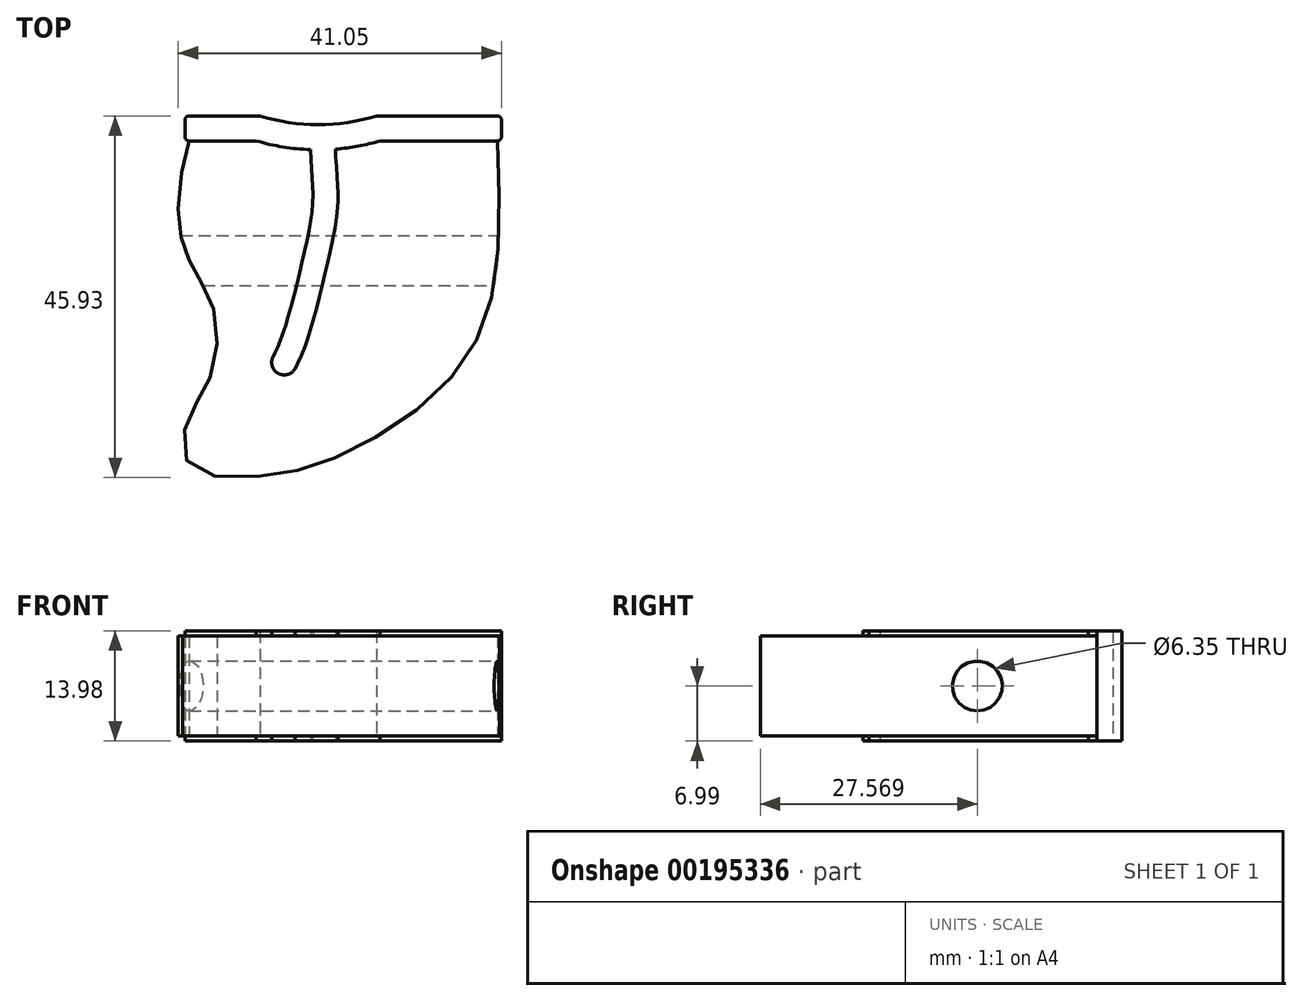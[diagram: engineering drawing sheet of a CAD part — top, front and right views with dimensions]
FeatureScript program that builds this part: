
annotation { "Feature Type Name" : "Feature", "Feature Type Description" : "" }
export const myFeature = defineFeature(function(context is Context, id is Id, definition is map)
    precondition{}
    {
        {
            var Q0;
            Q0=qCreatedBy(makeId("Top.planeOp"),FACE);
            var sketch = newSketch(context, id + "F0", { "sketchPlane" : qUnion([Q0])});
            skLineSegment(sketch, "E0", {"start": v(-17.53, 0) * mm, "end": v(-8.51, 0) * mm});
            skLineSegment(sketch, "E1", {"start": v(6.28, 0) * mm, "end": v(21.65, 0) * mm});
            skLineSegment(sketch, "E2.0", {"start": v(6.75, -3.17) * mm, "end": v(21.65, -3.17) * mm});
            skLineSegment(sketch, "E2.2", {"start": v(-17.53, -3.18) * mm, "end": v(-8.98, -3.18) * mm});
            skLineSegment(sketch, "E3", {"start": v(-18.04, -0.5) * mm, "end": v(-18.04, -2.67) * mm});
            skLineSegment(sketch, "E4", {"start": v(22.16, -0.5) * mm, "end": v(22.16, -2.67) * mm});
            skPoint(sketch, "E5.visualSharp", {"position": v(-18.04, -3.18) * mm});
            skArc(sketch, "E5.filletArc", {"start": v(-18.04, -2.67) * mm, "mid": v(-17.89, -3.03) * mm, "end": v(-17.53, -3.18) * mm});
            skPoint(sketch, "E6.visualSharp", {"position": v(-18.04, 0) * mm});
            skArc(sketch, "E6.filletArc", {"start": v(-17.53, 0) * mm, "mid": v(-17.89, -0.15) * mm, "end": v(-18.04, -0.5) * mm});
            skPoint(sketch, "E7.visualSharp", {"position": v(6.28, 0) * mm});
            skPoint(sketch, "E8.visualSharp", {"position": v(-8.51, 0) * mm});
            skPoint(sketch, "E9.visualSharp", {"position": v(22.16, 0) * mm});
            skArc(sketch, "E9.filletArc", {"start": v(22.16, -0.5) * mm, "mid": v(22, -0.15) * mm, "end": v(21.65, 0) * mm});
            skPoint(sketch, "E10.visualSharp", {"position": v(22.16, -3.17) * mm});
            skArc(sketch, "E10.filletArc", {"start": v(21.65, -3.17) * mm, "mid": v(22, -3.03) * mm, "end": v(22.16, -2.67) * mm});
            skFitSpline(sketch, "E11", {"points": [v(-2.09, -4.28) * mm, v(-1.8, -10.72) * mm, v(-3.13, -18.5) * mm, v(-5.58, -27.62) * mm, v(-6.9, -30.73) * mm], "startDerivative": vector(0.81, -30.4) * mm, "endDerivative": vector(-7.37, -14.95) * mm});
            skFitSpline(sketch, "E12.0", {"points": [v(1.09, -4.2) * mm, v(1.1, -4.78) * mm, v(1.16, -5.88) * mm, v(1.27, -7.2) * mm, v(1.34, -8.29) * mm, v(1.38, -9.13) * mm, v(1.4, -9.86) * mm, v(1.39, -10.46) * mm, v(1.37, -11.08) * mm, v(1.32, -11.85) * mm, v(1.2, -13.1) * mm, v(0.95, -14.66) * mm, v(0.57, -16.57) * mm, v(0.2, -18.2) * mm, v(-0.11, -19.55) * mm, v(-0.44, -20.93) * mm, v(-0.88, -22.7) * mm, v(-1.41, -24.78) * mm, v(-1.87, -26.4) * mm, v(-2.23, -27.61) * mm, v(-2.5, -28.46) * mm, v(-2.78, -29.23) * mm, v(-3.14, -30.16) * mm, v(-3.58, -31.16) * mm, v(-3.9, -31.82) * mm, v(-4.06, -32.13) * mm]});
            skArc(sketch, "E13", {"start": v(-6.9, -30.73) * mm, "mid": v(-6.13, -32.74) * mm, "end": v(-4.06, -32.13) * mm});
            skArc(sketch, "E14", {"start": v(-8.51, 0) * mm, "mid": v(-1.12, -1.13) * mm, "end": v(6.28, 0) * mm});
            skArc(sketch, "E15.0", {"start": v(-8.98, -3.18) * mm, "mid": v(-1.12, -4.3) * mm, "end": v(6.75, -3.18) * mm});
            skSolve(sketch);
        }
        {
            var Q0;
            Q0 = qSketchRegion(id + "F0", true);
            extrude(context, id + "F1", {"entities" : qUnion([Q0]), "endBound" : BoundingType.SYMMETRIC, "depth" : 13.97 * mm});
        }
        {
            var Q0;
            Q0=qCreatedBy(makeId("Top.planeOp"),FACE);
            var sketch = newSketch(context, id + "F2", { "sketchPlane" : qUnion([Q0])});
            skLineSegment(sketch, "E16", {"start": v(6.75, -3.17) * mm, "end": v(6.75, -3.17) * mm});
            skLineSegment(sketch, "E17", {"start": v(-17.53, -3.18) * mm, "end": v(-17.53, -3.18) * mm});
            skFitSpline(sketch, "E18", {"points": [v(-17.53, -3.18) * mm, v(-18.87, -11.15) * mm, v(-18.3, -16.34) * mm, v(-16.52, -20.17) * mm, v(-14.2, -25.3) * mm, v(-14.86, -33.3) * mm, v(-17.53, -38.15) * mm, v(-17.53, -44.2) * mm, v(-8.2, -45.76) * mm, v(2.25, -42.87) * mm, v(15.14, -33.98) * mm, v(21.14, -21.97) * mm, v(21.65, -3.17) * mm], "startDerivative": vector(-25.65, -67.95) * mm, "endDerivative": vector(-6.15, 159.47) * mm});
            skLineSegment(sketch, "E19", {"start": v(-17.53, -3.18) * mm, "end": v(-8.98, -3.18) * mm});
            skLineSegment(sketch, "E20", {"start": v(21.65, -3.18) * mm, "end": v(6.75, -3.17) * mm});
            skArc(sketch, "E21", {"start": v(-8.98, -3.18) * mm, "mid": v(-1.12, -4.18) * mm, "end": v(6.75, -3.17) * mm});
            skSolve(sketch);
        }
        {
            var Q0;
            Q0 = qSketchRegion(id + "F2", true);
            extrude(context, id + "F3", {"entities" : qUnion([Q0]), "operationType" : NewBodyOperationType.ADD, "endBound" : BoundingType.SYMMETRIC, "depth" : 12.7 * mm});
        }
        {
            var Q0;
            Q0=qCreatedBy(makeId("Right.planeOp"),FACE);
            var sketch = newSketch(context, id + "F4", { "sketchPlane" : qUnion([Q0])});
            skCircle(sketch, "E22", {"center": v(-18.36, 0) * mm, "radius": 3.18 * mm});
            skSolve(sketch);
        }
        {
            var Q0;
            Q0 = qSketchRegion(id + "F4", true);
            extrude(context, id + "F5", {"entities" : qUnion([Q0]), "operationType" : NewBodyOperationType.REMOVE, "endBound" : BoundingType.SYMMETRIC, "oppositeDirection" : true, "depth" : 50.8 * mm});
        }
    });
